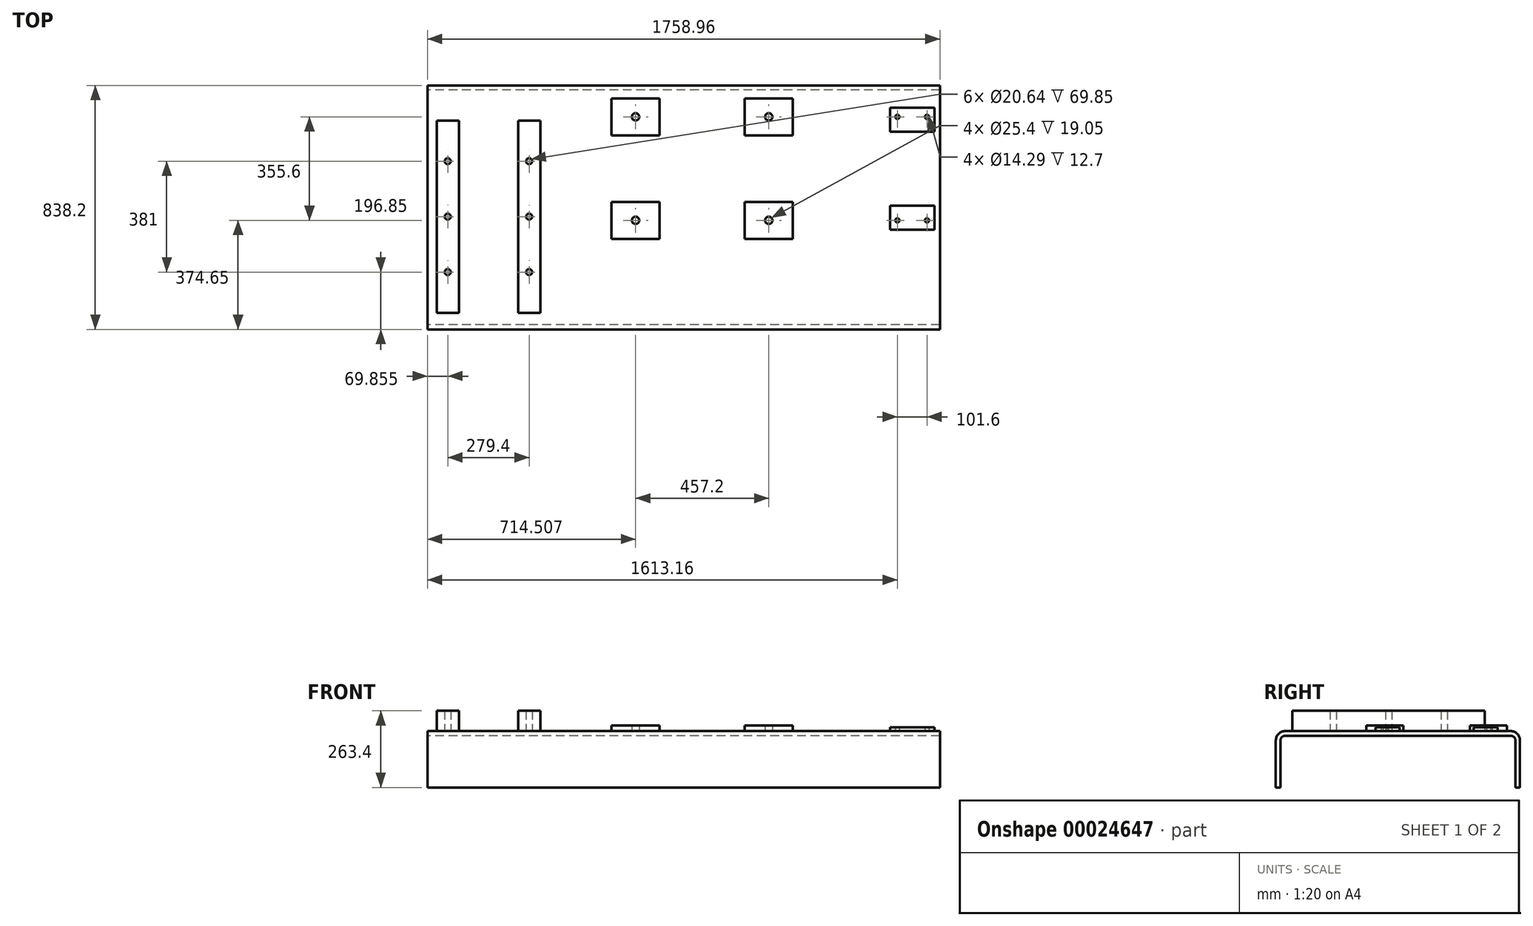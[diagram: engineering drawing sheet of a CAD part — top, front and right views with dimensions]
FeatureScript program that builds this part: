
annotation { "Feature Type Name" : "Feature", "Feature Type Description" : "" }
export const myFeature = defineFeature(function(context is Context, id is Id, definition is map)
    precondition{}
    {
        {
            var Q0;
            Q0=qCreatedBy(makeId("Right.planeOp"),FACE);
            var sketch = newSketch(context, id + "F0", { "sketchPlane" : qUnion([Q0])});
            skLineSegment(sketch, "E0", {"start": v(-126.98, 0) * mm, "end": v(108.74, 0) * mm, "construction": true});
            skLineSegment(sketch, "E1", {"start": v(0, 97.47) * mm, "end": v(0, -78.15) * mm, "construction": true});
            skLineSegment(sketch, "E2.0", {"start": v(-387.1, 193.55) * mm, "end": v(0, 193.55) * mm});
            skLineSegment(sketch, "E3.0", {"start": v(-419.1, 161.54) * mm, "end": v(-419.1, 0) * mm});
            skLineSegment(sketch, "E4.0", {"start": v(-387.1, 177.55) * mm, "end": v(0, 177.55) * mm});
            skLineSegment(sketch, "E5.0", {"start": v(-403.1, 161.54) * mm, "end": v(-403.1, 0) * mm});
            skArc(sketch, "E6.filletArc", {"start": v(-387.1, 177.55) * mm, "mid": v(-398.41, 172.86) * mm, "end": v(-403.1, 161.54) * mm});
            skPoint(sketch, "E7.visualSharp", {"position": v(-419.1, 193.55) * mm});
            skArc(sketch, "E7.filletArc", {"start": v(-387.1, 193.55) * mm, "mid": v(-409.73, 184.17) * mm, "end": v(-419.1, 161.54) * mm});
            skLineSegment(sketch, "E8", {"start": v(-419.1, 0) * mm, "end": v(-403.1, 0) * mm});
            skLineSegment(sketch, "E9.MirrorCS", {"start": v(419.1, 0) * mm, "end": v(403.1, 0) * mm});
            skArc(sketch, "E10.MirrorCS", {"start": v(387.1, 177.55) * mm, "mid": v(398.41, 172.86) * mm, "end": v(403.1, 161.54) * mm});
            skLineSegment(sketch, "E11.MirrorCS", {"start": v(387.1, 193.55) * mm, "end": v(0, 193.55) * mm});
            skArc(sketch, "E12.MirrorCS", {"start": v(387.1, 193.55) * mm, "mid": v(409.73, 184.17) * mm, "end": v(419.1, 161.54) * mm});
            skPoint(sketch, "E13.MirrorP", {"position": v(419.1, 193.55) * mm});
            skLineSegment(sketch, "E14.MirrorCS", {"start": v(387.1, 177.55) * mm, "end": v(0, 177.55) * mm});
            skLineSegment(sketch, "E15.MirrorCS", {"start": v(403.1, 161.54) * mm, "end": v(403.1, 0) * mm});
            skLineSegment(sketch, "E16.MirrorCS", {"start": v(419.1, 161.54) * mm, "end": v(419.1, 0) * mm});
            skSolve(sketch);
        }
        {
            var Q0;
            Q0=makeQuery(id+"F0.imprint","IMPRINT",FACE,{"disambiguationData":[TD([[makeQuery(id+"F0.imprint","IMPRINT",EDGE,{"derivedFrom":sQuery(id+"F0.wireOp",EDGE,"E2.0")}),-1.0]])]});
            extrude(context, id + "F1", {"entities" : qUnion([Q0]), "endBound" : BoundingType.SYMMETRIC, "depth" : 1758.95 * mm});
        }
        {
            var Q0;
            Q0=makeQuery(id+"F1.opExtrude","SWEPT_FACE",FACE,{"disambiguationData":[OSD([sQuery(id+"F0.wireOp",EDGE,"E2.0"),sQuery(id+"F0.wireOp",EDGE,"E11.MirrorCS")])]});
            var sketch = newSketch(context, id + "F2", { "sketchPlane" : qUnion([Q0])});
            skLineSegment(sketch, "E17.0", {"start": v(879.48, -419.1) * mm, "end": v(-879.48, -419.1) * mm, "construction": true});
            skLineSegment(sketch, "E18.0", {"start": v(879.48, -133.35) * mm, "end": v(-879.48, -133.35) * mm, "construction": true});
            skLineSegment(sketch, "E19.0", {"start": v(879.48, 133.35) * mm, "end": v(-879.48, 133.35) * mm, "construction": true});
            skLineSegment(sketch, "E20.0", {"start": v(-879.48, -387.1) * mm, "end": v(-879.48, 387.1) * mm, "construction": true});
            skLineSegment(sketch, "E21.0", {"start": v(-669.93, -387.1) * mm, "end": v(-669.93, 387.1) * mm, "construction": true});
            skLineSegment(sketch, "E22.0", {"start": v(63.63, -387.1) * mm, "end": v(63.63, 387.1) * mm, "construction": true});
            skLineSegment(sketch, "E23.0", {"start": v(784.48, -387.1) * mm, "end": v(784.48, 387.1) * mm, "construction": true});
            skLineSegment(sketch, "E24.0", {"start": v(-809.63, -387.1) * mm, "end": v(-809.63, 387.1) * mm, "construction": true});
            skLineSegment(sketch, "E25.0", {"start": v(-847.73, -387.1) * mm, "end": v(-847.73, 387.1) * mm, "construction": true});
            skLineSegment(sketch, "E26.0", {"start": v(879.48, -361.95) * mm, "end": v(-879.48, -361.95) * mm, "construction": true});
            skLineSegment(sketch, "E27.0", {"start": v(879.48, 298.45) * mm, "end": v(-879.48, 298.45) * mm, "construction": true});
            skLineSegment(sketch, "E28.bottom", {"start": v(-847.73, 298.45) * mm, "end": v(-809.63, 298.45) * mm});
            skLineSegment(sketch, "E28.top", {"start": v(-847.73, -361.95) * mm, "end": v(-809.63, -361.95) * mm});
            skLineSegment(sketch, "E28.left", {"start": v(-847.73, 298.45) * mm, "end": v(-847.73, -361.95) * mm});
            skLineSegment(sketch, "E28.right", {"start": v(-809.63, 298.45) * mm, "end": v(-809.63, -361.95) * mm, "construction": true});
            skLineSegment(sketch, "E29.MirrorCS", {"start": v(-771.53, 298.45) * mm, "end": v(-809.63, 298.45) * mm});
            skLineSegment(sketch, "E30.MirrorCS", {"start": v(-771.53, 298.45) * mm, "end": v(-771.53, -361.95) * mm});
            skLineSegment(sketch, "E31.MirrorCS", {"start": v(-771.53, -361.95) * mm, "end": v(-809.63, -361.95) * mm});
            skLineSegment(sketch, "E32.0", {"start": v(879.48, -222.25) * mm, "end": v(-879.48, -222.25) * mm, "construction": true});
            skCircle(sketch, "E33", {"center": v(-809.63, -222.25) * mm, "radius": 10.32 * mm});
            skCircle(sketch, "E34.0.1.0", {"center": v(-809.63, -31.75) * mm, "radius": 10.32 * mm});
            skCircle(sketch, "E34.0.2.0", {"center": v(-809.63, 158.75) * mm, "radius": 10.32 * mm});
            skLineSegment(sketch, "E34.direction1", {"start": v(-809.63, -222.25) * mm, "end": v(-784.23, -222.25) * mm, "construction": true});
            skLineSegment(sketch, "E34.direction2", {"start": v(-809.63, -222.25) * mm, "end": v(-809.63, -31.75) * mm, "construction": true});
            skLineSegment(sketch, "E35.MirrorCS", {"start": v(-568.33, 298.45) * mm, "end": v(-568.33, -361.95) * mm});
            skLineSegment(sketch, "E36.MirrorCS", {"start": v(-568.33, 298.45) * mm, "end": v(-530.23, 298.45) * mm});
            skLineSegment(sketch, "E37.MirrorCS", {"start": v(-492.13, 298.45) * mm, "end": v(-530.23, 298.45) * mm});
            skLineSegment(sketch, "E38.MirrorCS", {"start": v(-492.13, 298.45) * mm, "end": v(-492.13, -361.95) * mm});
            skCircle(sketch, "E39.MirrorC", {"center": v(-530.23, 158.75) * mm, "radius": 10.32 * mm});
            skCircle(sketch, "E40.MirrorC", {"center": v(-530.23, -31.75) * mm, "radius": 10.32 * mm});
            skCircle(sketch, "E41.MirrorC", {"center": v(-530.23, -222.25) * mm, "radius": 10.32 * mm});
            skLineSegment(sketch, "E42.MirrorCS", {"start": v(-2219.33, -222.25) * mm, "end": v(-460.38, -222.25) * mm});
            skLineSegment(sketch, "E43.MirrorCS", {"start": v(-2219.33, -133.35) * mm, "end": v(-460.38, -133.35) * mm});
            skLineSegment(sketch, "E44.MirrorCS", {"start": v(-568.33, -361.95) * mm, "end": v(-530.23, -361.95) * mm});
            skLineSegment(sketch, "E45.MirrorCS", {"start": v(-492.13, -361.95) * mm, "end": v(-530.23, -361.95) * mm});
            skSolve(sketch);
        }
        {
            var Q0;
            {var subQ6=sQuery(id+"F2.wireOp",EDGE,"E28.bottom");Q0=makeQuery(id+"F2.imprint","IMPRINT",FACE,{"disambiguationData":[TD([[makeQuery(id+"F2.imprint","IMPRINT",EDGE,{"derivedFrom":subQ6}),-1.0]])]});}
            var Q1;
            {var subQ6=sQuery(id+"F2.wireOp",EDGE,"E28.left");var subQ8=sQuery(id+"F2.wireOp",EDGE,"E43.MirrorCS");var subQ10=makeQuery(id+"F2.imprint","INTERSECT",VERTEX,{"derivedFrom":[subQ6,subQ8]});Q1=makeQuery(id+"F2.imprint","IMPRINT",FACE,{"disambiguationData":[TD([[makeQuery(id+"F2.imprint","IMPRINT",EDGE,{"disambiguationData":[TD([[subQ10,-1.0]])],"derivedFrom":subQ6}),1.0]])]});}
            var Q2;
            {var subQ9=sQuery(id+"F2.wireOp",EDGE,"E28.top");Q2=makeQuery(id+"F2.imprint","IMPRINT",FACE,{"disambiguationData":[TD([[makeQuery(id+"F2.imprint","IMPRINT",EDGE,{"derivedFrom":subQ9}),1.0]])]});}
            var Q3;
            {var subQ1=sQuery(id+"F2.wireOp",EDGE,"E44.MirrorCS");Q3=makeQuery(id+"F2.imprint","IMPRINT",FACE,{"disambiguationData":[TD([[makeQuery(id+"F2.imprint","IMPRINT",EDGE,{"derivedFrom":subQ1}),1.0]])]});}
            var Q4;
            {var subQ5=sQuery(id+"F2.wireOp",EDGE,"E43.MirrorCS");var subQ6=sQuery(id+"F2.wireOp",EDGE,"E35.MirrorCS");var subQ7=makeQuery(id+"F2.imprint","INTERSECT",VERTEX,{"derivedFrom":[subQ6,subQ5]});Q4=makeQuery(id+"F2.imprint","IMPRINT",FACE,{"disambiguationData":[TD([[makeQuery(id+"F2.imprint","IMPRINT",EDGE,{"disambiguationData":[TD([[subQ7,-1.0]])],"derivedFrom":subQ6}),1.0]])]});}
            var Q5;
            {var subQ6=sQuery(id+"F2.wireOp",EDGE,"E36.MirrorCS");Q5=makeQuery(id+"F2.imprint","IMPRINT",FACE,{"disambiguationData":[TD([[makeQuery(id+"F2.imprint","IMPRINT",EDGE,{"derivedFrom":subQ6}),-1.0]])]});}
            extrude(context, id + "F3", {"entities" : qUnion([Q0, Q1, Q2, Q3, Q4, Q5]), "operationType" : NewBodyOperationType.ADD, "depth" : 69.85 * mm});
        }
        {
            var Q0;
            {var subQ6=sQuery(id+"F2.wireOp",EDGE,"E28.bottom");Q0=makeQuery(id+"F2.imprint","IMPRINT",FACE,{"disambiguationData":[TD([[makeQuery(id+"F2.imprint","IMPRINT",EDGE,{"derivedFrom":subQ6}),1.0]])]});}
            var sketch = newSketch(context, id + "F4", { "sketchPlane" : qUnion([Q0])});
            skLineSegment(sketch, "E46.0", {"start": v(879.48, 133.35) * mm, "end": v(-879.48, 133.35) * mm, "construction": true});
            skLineSegment(sketch, "E47.0", {"start": v(63.63, -387.1) * mm, "end": v(63.63, 387.1) * mm, "construction": true});
            skLineSegment(sketch, "E48.0", {"start": v(879.48, 311.15) * mm, "end": v(-879.48, 311.15) * mm, "construction": true});
            skLineSegment(sketch, "E49.0", {"start": v(879.48, -44.45) * mm, "end": v(-879.48, -44.45) * mm, "construction": true});
            skLineSegment(sketch, "E50.0", {"start": v(-164.97, -387.1) * mm, "end": v(-164.97, 387.1) * mm, "construction": true});
            skLineSegment(sketch, "E51.0", {"start": v(-247.52, -387.1) * mm, "end": v(-247.52, 387.1) * mm, "construction": true});
            skLineSegment(sketch, "E52.0", {"start": v(879.48, -107.95) * mm, "end": v(-879.48, -107.95) * mm, "construction": true});
            skLineSegment(sketch, "E53.bottom", {"start": v(-247.52, -107.95) * mm, "end": v(-82.42, -107.95) * mm});
            skLineSegment(sketch, "E53.top", {"start": v(-247.52, 19.05) * mm, "end": v(-82.42, 19.05) * mm});
            skLineSegment(sketch, "E53.left", {"start": v(-247.52, -107.95) * mm, "end": v(-247.52, 19.05) * mm});
            skLineSegment(sketch, "E53.right", {"start": v(-82.42, -107.95) * mm, "end": v(-82.42, 19.05) * mm});
            skCircle(sketch, "E54", {"center": v(-164.97, -44.45) * mm, "radius": 12.7 * mm});
            skLineSegment(sketch, "E55.0.1.0", {"start": v(-247.52, 247.65) * mm, "end": v(-82.42, 247.65) * mm});
            skLineSegment(sketch, "E55.0.1.1", {"start": v(-247.52, 374.65) * mm, "end": v(-82.42, 374.65) * mm});
            skLineSegment(sketch, "E55.0.1.2", {"start": v(-247.52, 247.65) * mm, "end": v(-247.52, 374.65) * mm});
            skLineSegment(sketch, "E55.0.1.3", {"start": v(-82.42, 247.65) * mm, "end": v(-82.42, 374.65) * mm});
            skCircle(sketch, "E55.0.1.4", {"center": v(-164.97, 311.15) * mm, "radius": 12.7 * mm});
            skLineSegment(sketch, "E55.1.0.0", {"start": v(209.68, -107.95) * mm, "end": v(374.78, -107.95) * mm});
            skLineSegment(sketch, "E55.1.0.1", {"start": v(209.68, 19.05) * mm, "end": v(374.78, 19.05) * mm});
            skLineSegment(sketch, "E55.1.0.2", {"start": v(209.68, -107.95) * mm, "end": v(209.68, 19.05) * mm});
            skLineSegment(sketch, "E55.1.0.3", {"start": v(374.78, -107.95) * mm, "end": v(374.78, 19.05) * mm});
            skCircle(sketch, "E55.1.0.4", {"center": v(292.23, -44.45) * mm, "radius": 12.7 * mm});
            skLineSegment(sketch, "E55.1.1.0", {"start": v(209.68, 247.65) * mm, "end": v(374.78, 247.65) * mm});
            skLineSegment(sketch, "E55.1.1.1", {"start": v(209.68, 374.65) * mm, "end": v(374.78, 374.65) * mm});
            skLineSegment(sketch, "E55.1.1.2", {"start": v(209.68, 247.65) * mm, "end": v(209.68, 374.65) * mm});
            skLineSegment(sketch, "E55.1.1.3", {"start": v(374.78, 247.65) * mm, "end": v(374.78, 374.65) * mm});
            skCircle(sketch, "E55.1.1.4", {"center": v(292.23, 311.15) * mm, "radius": 12.7 * mm});
            skLineSegment(sketch, "E55.direction1", {"start": v(-247.52, -107.95) * mm, "end": v(209.68, -107.95) * mm, "construction": true});
            skLineSegment(sketch, "E55.direction2", {"start": v(-247.52, -107.95) * mm, "end": v(-247.52, 247.65) * mm, "construction": true});
            skSolve(sketch);
        }
        {
            var Q0;
            Q0=makeQuery(id+"F4.imprint","IMPRINT",FACE,{"disambiguationData":[TD([[makeQuery(id+"F4.imprint","IMPRINT",EDGE,{"derivedFrom":sQuery(id+"F4.wireOp",EDGE,"E55.0.1.0")}),1.0]])]});
            var Q1;
            Q1=makeQuery(id+"F4.imprint","IMPRINT",FACE,{"disambiguationData":[TD([[makeQuery(id+"F4.imprint","IMPRINT",EDGE,{"derivedFrom":sQuery(id+"F4.wireOp",EDGE,"E55.1.1.0")}),1.0]])]});
            var Q2;
            Q2=makeQuery(id+"F4.imprint","IMPRINT",FACE,{"disambiguationData":[TD([[makeQuery(id+"F4.imprint","IMPRINT",EDGE,{"derivedFrom":sQuery(id+"F4.wireOp",EDGE,"E55.1.0.0")}),1.0]])]});
            var Q3;
            Q3=makeQuery(id+"F4.imprint","IMPRINT",FACE,{"disambiguationData":[TD([[makeQuery(id+"F4.imprint","IMPRINT",EDGE,{"derivedFrom":sQuery(id+"F4.wireOp",EDGE,"E53.bottom")}),1.0]])]});
            extrude(context, id + "F5", {"entities" : qUnion([Q0, Q1, Q2, Q3]), "operationType" : NewBodyOperationType.ADD, "depth" : 19.05 * mm});
        }
        {
            var Q0;
            {var subQ6=sQuery(id+"F2.wireOp",EDGE,"E28.bottom");Q0=makeQuery(id+"F2.imprint","IMPRINT",FACE,{"disambiguationData":[TD([[makeQuery(id+"F2.imprint","IMPRINT",EDGE,{"derivedFrom":subQ6}),1.0]])]});}
            var sketch = newSketch(context, id + "F6", { "sketchPlane" : qUnion([Q0])});
            skLineSegment(sketch, "E56.0", {"start": v(784.48, -387.1) * mm, "end": v(784.48, 387.1) * mm, "construction": true});
            skLineSegment(sketch, "E57.0", {"start": v(879.48, 133.35) * mm, "end": v(-879.48, 133.35) * mm, "construction": true});
            skLineSegment(sketch, "E58.0", {"start": v(860.68, -387.1) * mm, "end": v(860.68, 387.1) * mm, "construction": true});
            skCircle(sketch, "E59.0", {"center": v(292.23, -44.45) * mm, "radius": 12.7 * mm, "construction": true});
            skLineSegment(sketch, "E60", {"start": v(292.23, -44.45) * mm, "end": v(906.76, -44.45) * mm, "construction": true});
            skLineSegment(sketch, "E61.0", {"start": v(292.23, 6.35) * mm, "end": v(906.76, 6.35) * mm, "construction": true});
            skLineSegment(sketch, "E62.bottom", {"start": v(860.68, 6.35) * mm, "end": v(708.28, 6.35) * mm});
            skLineSegment(sketch, "E62.top", {"start": v(860.68, -76.2) * mm, "end": v(708.28, -76.2) * mm});
            skLineSegment(sketch, "E62.left", {"start": v(860.68, 6.35) * mm, "end": v(860.68, -76.2) * mm});
            skLineSegment(sketch, "E62.right", {"start": v(708.28, 6.35) * mm, "end": v(708.28, -76.2) * mm});
            skLineSegment(sketch, "E63.0", {"start": v(835.28, -387.1) * mm, "end": v(835.28, 387.1) * mm, "construction": true});
            skLineSegment(sketch, "E64.0", {"start": v(733.68, -387.1) * mm, "end": v(733.68, 387.1) * mm, "construction": true});
            skCircle(sketch, "E65", {"center": v(733.68, -44.45) * mm, "radius": 7.14 * mm});
            skCircle(sketch, "E66", {"center": v(835.28, -44.45) * mm, "radius": 7.14 * mm});
            skCircle(sketch, "E67.MirrorC", {"center": v(733.68, 311.15) * mm, "radius": 7.14 * mm});
            skCircle(sketch, "E68.MirrorC", {"center": v(835.28, 311.15) * mm, "radius": 7.14 * mm});
            skLineSegment(sketch, "E69.MirrorCS", {"start": v(860.68, 260.35) * mm, "end": v(860.68, 342.9) * mm});
            skLineSegment(sketch, "E70.MirrorCS", {"start": v(708.28, 260.35) * mm, "end": v(708.28, 342.9) * mm});
            skLineSegment(sketch, "E71.MirrorCS", {"start": v(860.68, 260.35) * mm, "end": v(708.28, 260.35) * mm});
            skLineSegment(sketch, "E72.MirrorCS", {"start": v(860.68, 342.9) * mm, "end": v(708.28, 342.9) * mm});
            skSolve(sketch);
        }
        {
            var Q0;
            Q0 = qSketchRegion(id + "F6", true);
            extrude(context, id + "F7", {"entities" : qUnion([Q0]), "operationType" : NewBodyOperationType.ADD, "depth" : 12.7 * mm});
        }
    });
